# Revit family: 99058_HOST_FACE
name_source: partatom
category: Lighting Fixtures
units: mm (PartAtom-declared; Revit-internal decimal feet)

## family parameters
Cut with Voids When Loaded = Yes
Host = Face
Light Source = Yes
Part Type = Normal
Room Calculation Point = No
Round Connector Dimension = Use Diameter
Shared = No

## types (4) — shared parameters
Color Filter = 16777215
Dimming Lamp Color Temperature Shift = <None>
Manufacturer = BEGA-US
Telephone = 805.684.0533
Tilt Angle = 90.00°
URL = www.bega-us.com

## per-type parameters (varying)
| type | Default Elevation | Description | Lamp | Model | Photometric Web File |
| Wall Luminaires - Directed Light | 6' - 0" | Surface wall with cutoff optics | 44.6W LED | 2260LED | generic |
| Wall Luminaires - Linear | 6' - 0" | Suface wall - linear with white acrylic diffuser | (1) 39W CF twin-4-p | 4425P | generic |
| Bollards | 0' - 0" | LED bollard with fully shielded light source | 18.9W LED | 99 058 | 99058K4.ies |
| Shieleded LED Bollard with asymmetric light distribution on one side | 0' - 0" | Shielded LED Bollard with asymmetric light distribuiton on one side | 18.9W LED | 99 058 | 99058K4.ies |

## geometry (parser evidence)
native form markers: Blend x8, Sweep x9
no freeform markers — native parametric forms only
